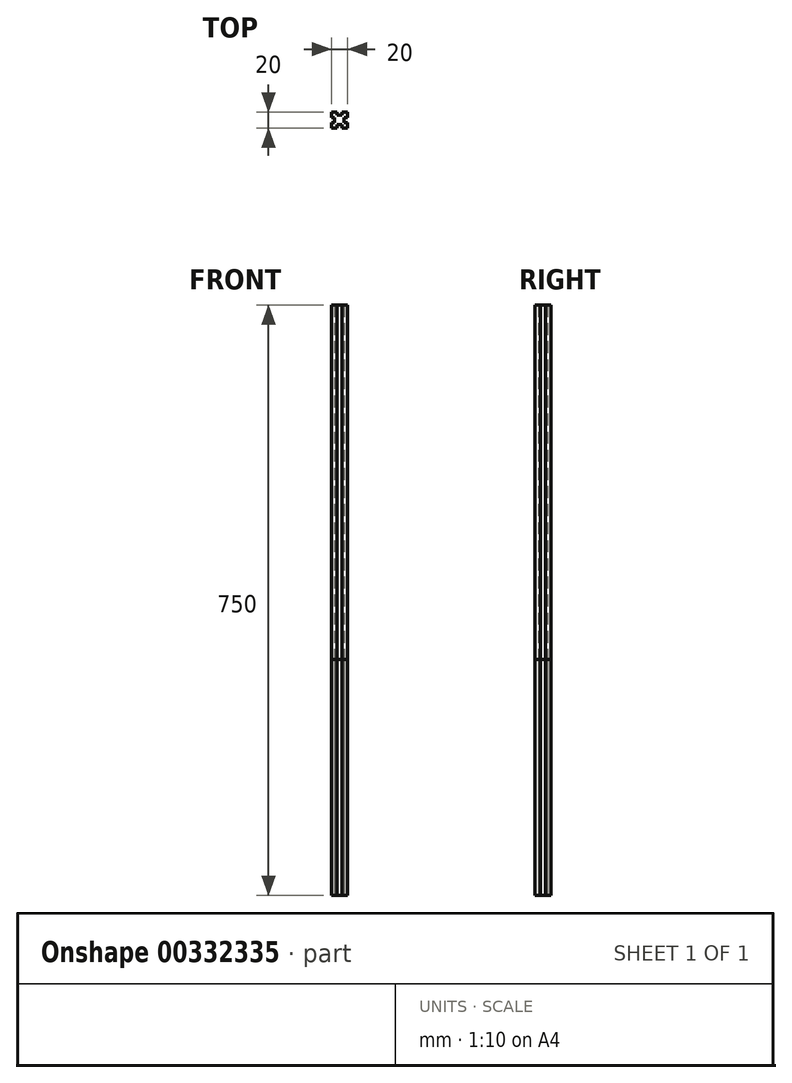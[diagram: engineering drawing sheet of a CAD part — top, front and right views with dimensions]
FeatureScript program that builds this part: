
annotation { "Feature Type Name" : "Feature", "Feature Type Description" : "" }
export const myFeature = defineFeature(function(context is Context, id is Id, definition is map)
    precondition{}
    {
        {
            var Q0;
            Q0=qCreatedBy(makeId("Top.planeOp"),FACE);
            var sketch = newSketch(context, id + "F0", { "sketchPlane" : qUnion([Q0])});
            skLineSegment(sketch, "E0.bottom", {"start": v(10, -10) * mm, "end": v(3, -10) * mm});
            skLineSegment(sketch, "E0.top", {"start": v(10, 10) * mm, "end": v(3, 10) * mm});
            skLineSegment(sketch, "E0.left", {"start": v(10, -10) * mm, "end": v(10, -3) * mm});
            skLineSegment(sketch, "E0.right", {"start": v(-10, -10) * mm, "end": v(-10, -3) * mm});
            skPoint(sketch, "E0.middle", {"position": v(0, 0) * mm});
            skLineSegment(sketch, "E1.bottom", {"start": v(10, -3) * mm, "end": v(6, -3) * mm});
            skLineSegment(sketch, "E1.top", {"start": v(10, 3) * mm, "end": v(6, 3) * mm});
            skLineSegment(sketch, "E2.left", {"start": v(3, -10) * mm, "end": v(3, -6) * mm});
            skLineSegment(sketch, "E2.right", {"start": v(-3, -10) * mm, "end": v(-3, -6) * mm});
            skLineSegment(sketch, "E3.0", {"start": v(3, 6) * mm, "end": v(-3, 6) * mm});
            skLineSegment(sketch, "E4.0", {"start": v(6, -3) * mm, "end": v(6, 3) * mm});
            skLineSegment(sketch, "E5.0", {"start": v(3, -6) * mm, "end": v(-3, -6) * mm});
            skLineSegment(sketch, "E6.0", {"start": v(-6, -3) * mm, "end": v(-6, 3) * mm});
            skLineSegment(sketch, "E7.trimOffspring", {"start": v(-6, 3) * mm, "end": v(-10, 3) * mm});
            skLineSegment(sketch, "E8.trimOffspring", {"start": v(-3, 6) * mm, "end": v(-3, 10) * mm});
            skLineSegment(sketch, "E9.trimOffspring", {"start": v(3, 6) * mm, "end": v(3, 10) * mm});
            skLineSegment(sketch, "E10.trimOffspring", {"start": v(-6, -3) * mm, "end": v(-10, -3) * mm});
            skLineSegment(sketch, "E11.trimOffspring", {"start": v(10, 3) * mm, "end": v(10, 10) * mm});
            skLineSegment(sketch, "E12.trimOffspring", {"start": v(-3, 10) * mm, "end": v(-10, 10) * mm});
            skLineSegment(sketch, "E13.trimOffspring", {"start": v(-10, 3) * mm, "end": v(-10, 10) * mm});
            skLineSegment(sketch, "E14.trimOffspring", {"start": v(-3, -10) * mm, "end": v(-10, -10) * mm});
            skSolve(sketch);
        }
        {
            var Q0;
            Q0 = qSketchRegion(id + "F0", true);
            extrude(context, id + "F1", {"entities" : qUnion([Q0]), "depth" : 750 * mm});
        }
        {
            var Q0;
            Q0=makeQuery(id+"F0.imprint","IMPRINT",FACE,{"disambiguationData":[TD([[makeQuery(id+"F0.imprint","IMPRINT",EDGE,{"derivedFrom":sQuery(id+"F0.wireOp",EDGE,"E0.bottom")}),-1.0]])]});
            extrude(context, id + "F2", {"entities" : qUnion([Q0]), "depth" : 300 * mm});
        }
    });
